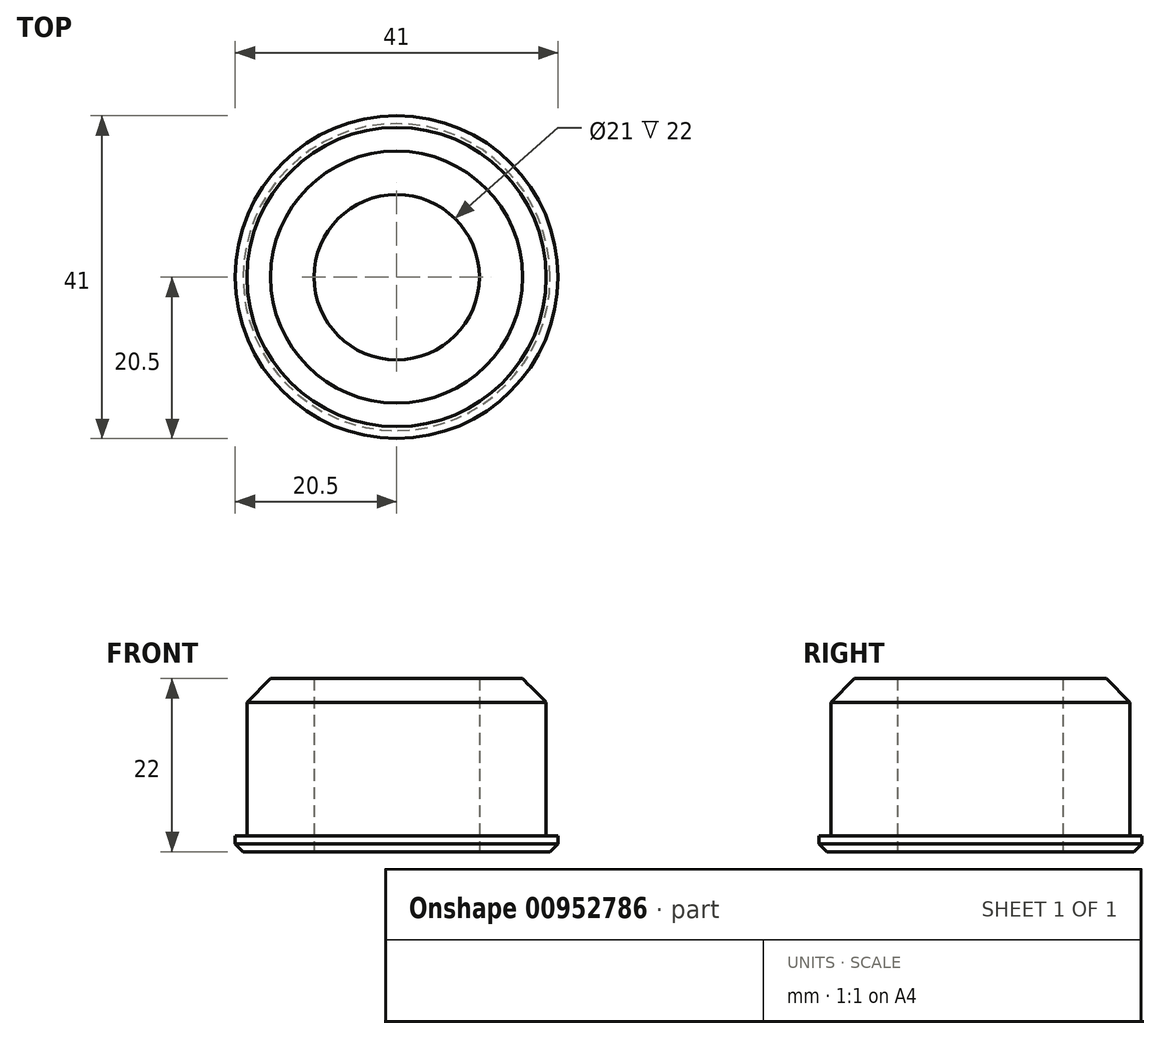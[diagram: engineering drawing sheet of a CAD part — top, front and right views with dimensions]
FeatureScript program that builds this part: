
annotation { "Feature Type Name" : "Feature", "Feature Type Description" : "" }
export const myFeature = defineFeature(function(context is Context, id is Id, definition is map)
    precondition{}
    {
        {
            var Q0;
            Q0=qCreatedBy(makeId("Top.planeOp"),FACE);
            var sketch = newSketch(context, id + "F0", { "sketchPlane" : qUnion([Q0])});
            skCircle(sketch, "E0", {"center": v(0, 0) * mm, "radius": 20.5 * mm});
            skSolve(sketch);
        }
        {
            var Q0;
            Q0 = qSketchRegion(id + "F0", true);
            extrude(context, id + "F1", {"entities" : qUnion([Q0]), "depth" : 2 * mm, "offsetDistance" : 25 * mm});
        }
        {
            var Q0;
            Q0=makeQuery(id+"F1.opExtrude","CAP_FACE",FACE,{"disambiguationData":[OSD([sQuery(id+"F0.wireOp",EDGE,"E0")])],"isStart":false});
            var sketch = newSketch(context, id + "F2", { "sketchPlane" : qUnion([Q0])});
            skCircle(sketch, "E1", {"center": v(0, 0) * mm, "radius": 19 * mm});
            skSolve(sketch);
        }
        {
            var Q0;
            Q0 = qSketchRegion(id + "F2", true);
            extrude(context, id + "F3", {"entities" : qUnion([Q0]), "operationType" : NewBodyOperationType.ADD, "depth" : 20 * mm, "offsetDistance" : 25 * mm});
        }
        {
            var Q0;
            Q0=sQuery(id+"F0.wireOp",VERTEX,"E0.center");
            var Q1;
            Q1=makeQuery(id+"F1.opExtrude","SWEPT_BODY",BODY,{"disambiguationData":[OSD([sQuery(id+"F0.wireOp",EDGE,"E0")])]});
            hole(context, id + "F4", {"style" : HoleStyle.SIMPLE, "endStyle" : HoleEndStyle.THROUGH, "oppositeDirection" : true, "holeDiameter" : 21 * mm, "majorDiameter" : 5 * mm, "isTappedThrough" : true, "tappedDepth" : 12 * mm, "tapClearance" : 3, "startFromSketch" : true, "locations" : qUnion([Q0]), "scope" : qUnion([Q1])});
        }
        {
            var Q0;
            Q0=makeQuery(id+"F4.hole-0.boolean.opBoolean","INTERSECT",EDGE,{"derivedFrom":[makeQuery(id+"F3.opExtrude","CAP_FACE",FACE,{"disambiguationData":[OSD([sQuery(id+"F2.wireOp",EDGE,"E1")])],"isStart":false}),makeQuery(id+"F4.hole-0.opRevolve","SWEPT_FACE",FACE,{"disambiguationData":[OSD([sQuery(id+"F4.hole-0.sketch.wireOp",EDGE,"core_line_2")])]})]});
            var Q1;
            Q1=makeQuery(id+"F4.hole-0.boolean.opBoolean","COPY",EDGE,{"derivedFrom":makeQuery(id+"F4.hole-0.opRevolve","SWEPT_EDGE",EDGE,{"disambiguationData":[OSD([sQuery(id+"F4.hole-0.sketch.wireOp",EDGE,"core_line_2"),sQuery(id+"F4.hole-0.sketch.wireOp",EDGE,"core_line_3")])]})});
            var Q2;
            Q2=makeQuery(id+"F1.opExtrude","CAP_EDGE",EDGE,{"disambiguationData":[OSD([sQuery(id+"F0.wireOp",EDGE,"E0")])],"isStart":true});
            chamfer(context, id + "F5", {"entities" : qUnion([Q0, Q1, Q2]), "width" : 1 * mm, "tangentPropagation" : true});
        }
        {
            var Q0;
            Q0=makeQuery(id+"F3.opExtrude","CAP_EDGE",EDGE,{"disambiguationData":[OSD([sQuery(id+"F2.wireOp",EDGE,"E1")])],"isStart":false});
            chamfer(context, id + "F6", {"entities" : qUnion([Q0]), "width" : 3 * mm, "tangentPropagation" : true});
        }
    });
